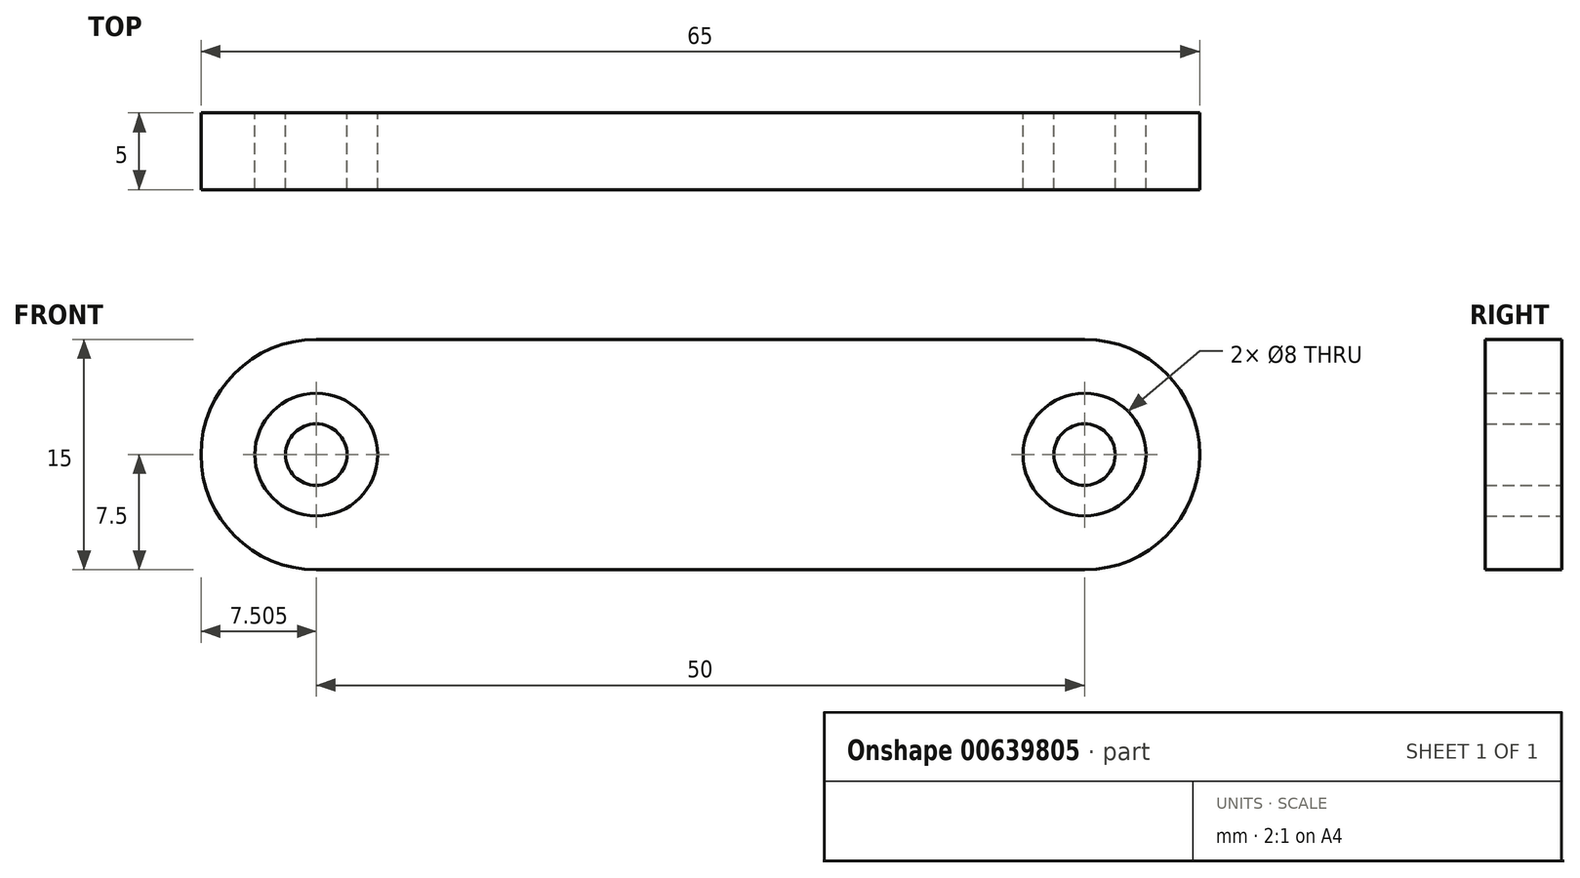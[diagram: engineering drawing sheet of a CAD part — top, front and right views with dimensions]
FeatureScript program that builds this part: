
annotation { "Feature Type Name" : "Feature", "Feature Type Description" : "" }
export const myFeature = defineFeature(function(context is Context, id is Id, definition is map)
    precondition{}
    {
        {
            var Q0;
            Q0=qCreatedBy(makeId("Front.planeOp"),FACE);
            var sketch = newSketch(context, id + "F0", { "sketchPlane" : qUnion([Q0])});
            skArc(sketch, "E0", {"start": v(-5.17, 7.5) * mm, "mid": v(-12.67, 0) * mm, "end": v(-5.17, -7.5) * mm});
            skArc(sketch, "E1", {"start": v(44.83, -7.5) * mm, "mid": v(52.33, 0) * mm, "end": v(44.83, 7.5) * mm});
            skCircle(sketch, "E2", {"center": v(44.83, 0) * mm, "radius": 4 * mm});
            skCircle(sketch, "E3", {"center": v(44.83, 0) * mm, "radius": 2 * mm});
            skCircle(sketch, "E4", {"center": v(-5.17, 0) * mm, "radius": 4 * mm});
            skCircle(sketch, "E5", {"center": v(-5.17, 0) * mm, "radius": 2 * mm});
            skLineSegment(sketch, "E6", {"start": v(-5.17, 7.5) * mm, "end": v(44.83, 7.5) * mm});
            skLineSegment(sketch, "E7", {"start": v(-5.17, -7.5) * mm, "end": v(44.83, -7.5) * mm});
            skSolve(sketch);
        }
        {
            var Q0;
            Q0=makeQuery(id+"F0.imprint","IMPRINT",FACE,{"disambiguationData":[TD([[makeQuery(id+"F0.imprint","IMPRINT",EDGE,{"derivedFrom":sQuery(id+"F0.wireOp",EDGE,"E0")}),1.0]])]});
            var Q1;
            Q1=makeQuery(id+"F0.imprint","IMPRINT",FACE,{"disambiguationData":[TD([[makeQuery(id+"F0.imprint","IMPRINT",EDGE,{"derivedFrom":sQuery(id+"F0.wireOp",EDGE,"E3")}),1.0]])]});
            var Q2;
            Q2=makeQuery(id+"F0.imprint","IMPRINT",FACE,{"disambiguationData":[TD([[makeQuery(id+"F0.imprint","IMPRINT",EDGE,{"derivedFrom":sQuery(id+"F0.wireOp",EDGE,"E5")}),1.0]])]});
            extrude(context, id + "F1", {"entities" : qUnion([Q0, Q1, Q2]), "depth" : 5 * mm, "offsetDistance" : 25.4 * mm});
        }
    });
